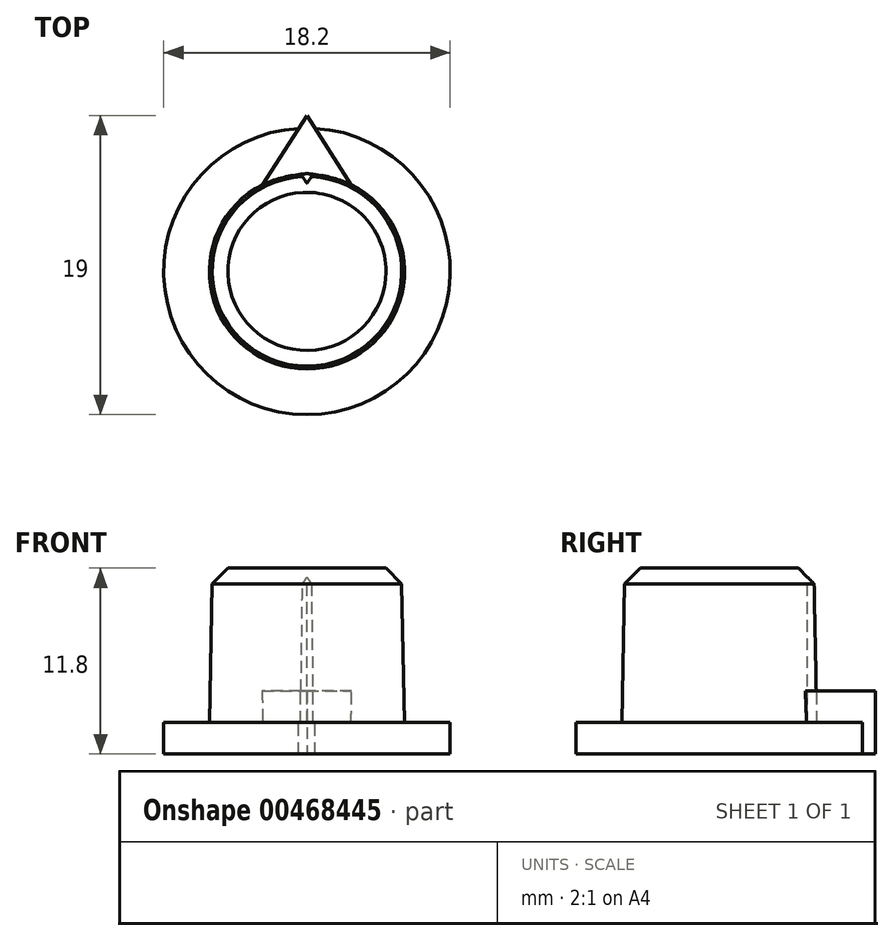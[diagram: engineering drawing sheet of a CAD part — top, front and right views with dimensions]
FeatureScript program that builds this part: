
annotation { "Feature Type Name" : "Feature", "Feature Type Description" : "" }
export const myFeature = defineFeature(function(context is Context, id is Id, definition is map)
    precondition{}
    {
        {
            var Q0;
            Q0=qCreatedBy(makeId("Right.planeOp"),FACE);
            var sketch = newSketch(context, id + "F0", { "sketchPlane" : qUnion([Q0])});
            skLineSegment(sketch, "E0", {"start": v(-9.1, 0) * mm, "end": v(-9.1, 2) * mm});
            skLineSegment(sketch, "E1", {"start": v(-9.1, 2) * mm, "end": v(-6.2, 2) * mm});
            skLineSegment(sketch, "E2", {"start": v(-6.2, 2) * mm, "end": v(-6.02, 10.8) * mm});
            skLineSegment(sketch, "E3", {"start": v(-5.02, 11.8) * mm, "end": v(0, 11.8) * mm});
            skLineSegment(sketch, "E4", {"start": v(0, 11.8) * mm, "end": v(0, 0) * mm});
            skLineSegment(sketch, "E5", {"start": v(0, 0) * mm, "end": v(-9.1, 0) * mm});
            skLineSegment(sketch, "E6", {"start": v(-6.02, 10.8) * mm, "end": v(-5.02, 11.8) * mm});
            skPoint(sketch, "E7.orphan", {"position": v(-6, 11.8) * mm});
            skSolve(sketch);
        }
        {
            var Q0;
            Q0=makeQuery(id+"F0.imprint","IMPRINT",FACE,{"disambiguationData":[TD([[makeQuery(id+"F0.imprint","IMPRINT",EDGE,{"derivedFrom":sQuery(id+"F0.wireOp",EDGE,"E0")}),-1.0]])]});
            var Q1;
            Q1=sQuery(id+"F0.wireOp",EDGE,"E4");
            revolve(context, id + "F1", {"entities" : qUnion([Q0]), "axis" : qUnion([Q1]), "revolveType" : RevolveType.FULL});
        }
        {
            var Q0;
            Q0=makeQuery(id+"F1.opRevolve","SWEPT_FACE",FACE,{"disambiguationData":[OSD([sQuery(id+"F0.wireOp",EDGE,"E3")])]});
            var sketch = newSketch(context, id + "F2", { "sketchPlane" : qUnion([Q0])});
            skLineSegment(sketch, "E8", {"start": v(0, 5.6) * mm, "end": v(-0.4, 6.19) * mm});
            skLineSegment(sketch, "E9", {"start": v(0.4, 6.19) * mm, "end": v(0, 5.6) * mm});
            skLineSegment(sketch, "E10", {"start": v(0, 0) * mm, "end": v(0, 6.2) * mm, "construction": true});
            skArc(sketch, "E11.2", {"start": v(0.4, 6.19) * mm, "mid": v(0, 6.2) * mm, "end": v(-0.4, 6.19) * mm});
            skSolve(sketch);
        }
        {
            var Q0;
            {var subQ0=sQuery(id+"F0.wireOp",EDGE,"E1");Q0=makeQuery(id+"Fq8YrrvR0LvIwax_1.47.F6.boolean.opBoolean","MERGE",FACE,{"derivedFrom":[makeQuery(id+"Fq8YrrvR0LvIwax_1.46.F6.boolean.opBoolean","MERGE",FACE,{"derivedFrom":[makeQuery(id+"Fq8YrrvR0LvIwax_1.45.F6.boolean.opBoolean","MERGE",FACE,{"derivedFrom":[makeQuery(id+"Fq8YrrvR0LvIwax_1.44.F6.boolean.opBoolean","MERGE",FACE,{"derivedFrom":[makeQuery(id+"Fq8YrrvR0LvIwax_1.43.F6.boolean.opBoolean","MERGE",FACE,{"derivedFrom":[makeQuery(id+"Fq8YrrvR0LvIwax_1.42.F6.boolean.opBoolean","MERGE",FACE,{"derivedFrom":[makeQuery(id+"Fq8YrrvR0LvIwax_1.41.F6.boolean.opBoolean","MERGE",FACE,{"derivedFrom":[makeQuery(id+"Fq8YrrvR0LvIwax_1.40.F6.boolean.opBoolean","MERGE",FACE,{"derivedFrom":[makeQuery(id+"Fq8YrrvR0LvIwax_1.39.F6.boolean.opBoolean","MERGE",FACE,{"derivedFrom":[makeQuery(id+"Fq8YrrvR0LvIwax_1.38.F6.boolean.opBoolean","MERGE",FACE,{"derivedFrom":[makeQuery(id+"Fq8YrrvR0LvIwax_1.37.F6.boolean.opBoolean","MERGE",FACE,{"derivedFrom":[makeQuery(id+"Fq8YrrvR0LvIwax_1.36.F6.boolean.opBoolean","MERGE",FACE,{"derivedFrom":[makeQuery(id+"Fq8YrrvR0LvIwax_1.35.F6.boolean.opBoolean","MERGE",FACE,{"derivedFrom":[makeQuery(id+"Fq8YrrvR0LvIwax_1.34.F6.boolean.opBoolean","MERGE",FACE,{"derivedFrom":[makeQuery(id+"Fq8YrrvR0LvIwax_1.33.F6.boolean.opBoolean","MERGE",FACE,{"derivedFrom":[makeQuery(id+"Fq8YrrvR0LvIwax_1.32.F6.boolean.opBoolean","MERGE",FACE,{"derivedFrom":[makeQuery(id+"Fq8YrrvR0LvIwax_1.31.F6.boolean.opBoolean","MERGE",FACE,{"derivedFrom":[makeQuery(id+"Fq8YrrvR0LvIwax_1.30.F6.boolean.opBoolean","MERGE",FACE,{"derivedFrom":[makeQuery(id+"Fq8YrrvR0LvIwax_1.29.F6.boolean.opBoolean","MERGE",FACE,{"derivedFrom":[makeQuery(id+"Fq8YrrvR0LvIwax_1.28.F6.boolean.opBoolean","MERGE",FACE,{"derivedFrom":[makeQuery(id+"Fq8YrrvR0LvIwax_1.27.F6.boolean.opBoolean","MERGE",FACE,{"derivedFrom":[makeQuery(id+"Fq8YrrvR0LvIwax_1.26.F6.boolean.opBoolean","MERGE",FACE,{"derivedFrom":[makeQuery(id+"Fq8YrrvR0LvIwax_1.25.F6.boolean.opBoolean","MERGE",FACE,{"derivedFrom":[makeQuery(id+"Fq8YrrvR0LvIwax_1.24.F6.boolean.opBoolean","MERGE",FACE,{"derivedFrom":[makeQuery(id+"Fq8YrrvR0LvIwax_1.23.F6.boolean.opBoolean","MERGE",FACE,{"derivedFrom":[makeQuery(id+"Fq8YrrvR0LvIwax_1.22.F6.boolean.opBoolean","MERGE",FACE,{"derivedFrom":[makeQuery(id+"Fq8YrrvR0LvIwax_1.21.F6.boolean.opBoolean","MERGE",FACE,{"derivedFrom":[makeQuery(id+"Fq8YrrvR0LvIwax_1.20.F6.boolean.opBoolean","MERGE",FACE,{"derivedFrom":[makeQuery(id+"Fq8YrrvR0LvIwax_1.19.F6.boolean.opBoolean","MERGE",FACE,{"derivedFrom":[makeQuery(id+"Fq8YrrvR0LvIwax_1.18.F6.boolean.opBoolean","MERGE",FACE,{"derivedFrom":[makeQuery(id+"Fq8YrrvR0LvIwax_1.17.F6.boolean.opBoolean","MERGE",FACE,{"derivedFrom":[makeQuery(id+"Fq8YrrvR0LvIwax_1.16.F6.boolean.opBoolean","MERGE",FACE,{"derivedFrom":[makeQuery(id+"Fq8YrrvR0LvIwax_1.15.F6.boolean.opBoolean","MERGE",FACE,{"derivedFrom":[makeQuery(id+"Fq8YrrvR0LvIwax_1.14.F6.boolean.opBoolean","MERGE",FACE,{"derivedFrom":[makeQuery(id+"Fq8YrrvR0LvIwax_1.13.F6.boolean.opBoolean","MERGE",FACE,{"derivedFrom":[makeQuery(id+"Fq8YrrvR0LvIwax_1.12.F6.boolean.opBoolean","MERGE",FACE,{"derivedFrom":[makeQuery(id+"Fq8YrrvR0LvIwax_1.11.F6.boolean.opBoolean","MERGE",FACE,{"derivedFrom":[makeQuery(id+"Fq8YrrvR0LvIwax_1.10.F6.boolean.opBoolean","MERGE",FACE,{"derivedFrom":[makeQuery(id+"Fq8YrrvR0LvIwax_1.9.F6.boolean.opBoolean","MERGE",FACE,{"derivedFrom":[makeQuery(id+"Fq8YrrvR0LvIwax_1.8.F6.boolean.opBoolean","MERGE",FACE,{"derivedFrom":[makeQuery(id+"Fq8YrrvR0LvIwax_1.7.F6.boolean.opBoolean","MERGE",FACE,{"derivedFrom":[makeQuery(id+"Fq8YrrvR0LvIwax_1.6.F6.boolean.opBoolean","MERGE",FACE,{"derivedFrom":[makeQuery(id+"Fq8YrrvR0LvIwax_1.5.F6.boolean.opBoolean","MERGE",FACE,{"derivedFrom":[makeQuery(id+"Fq8YrrvR0LvIwax_1.4.F6.boolean.opBoolean","MERGE",FACE,{"derivedFrom":[makeQuery(id+"Fq8YrrvR0LvIwax_1.3.F6.boolean.opBoolean","MERGE",FACE,{"derivedFrom":[makeQuery(id+"Fq8YrrvR0LvIwax_1.2.F6.boolean.opBoolean","MERGE",FACE,{"derivedFrom":[makeQuery(id+"Fq8YrrvR0LvIwax_1.1.F6.boolean.opBoolean","MERGE",FACE,{"derivedFrom":[makeQuery(id+"F6.boolean.opBoolean","MERGE",FACE,{"derivedFrom":[makeQuery(id+"F1.opRevolve","SWEPT_FACE",FACE,{"disambiguationData":[OSD([subQ0])]}),makeQuery(id+"F6.opExtrude","CAP_FACE",FACE,{"disambiguationData":[OSD([subQ0])],"isStart":false})]}),makeQuery(id+"Fq8YrrvR0LvIwax_1.1.F6.opExtrude","CAP_FACE",FACE,{"disambiguationData":[OSD([subQ0])],"isStart":false})]}),makeQuery(id+"Fq8YrrvR0LvIwax_1.2.F6.opExtrude","CAP_FACE",FACE,{"disambiguationData":[OSD([subQ0])],"isStart":false})]}),makeQuery(id+"Fq8YrrvR0LvIwax_1.3.F6.opExtrude","CAP_FACE",FACE,{"disambiguationData":[OSD([subQ0])],"isStart":false})]}),makeQuery(id+"Fq8YrrvR0LvIwax_1.4.F6.opExtrude","CAP_FACE",FACE,{"disambiguationData":[OSD([subQ0])],"isStart":false})]}),makeQuery(id+"Fq8YrrvR0LvIwax_1.5.F6.opExtrude","CAP_FACE",FACE,{"disambiguationData":[OSD([subQ0])],"isStart":false})]}),makeQuery(id+"Fq8YrrvR0LvIwax_1.6.F6.opExtrude","CAP_FACE",FACE,{"disambiguationData":[OSD([subQ0])],"isStart":false})]}),makeQuery(id+"Fq8YrrvR0LvIwax_1.7.F6.opExtrude","CAP_FACE",FACE,{"disambiguationData":[OSD([subQ0])],"isStart":false})]}),makeQuery(id+"Fq8YrrvR0LvIwax_1.8.F6.opExtrude","CAP_FACE",FACE,{"disambiguationData":[OSD([subQ0])],"isStart":false})]}),makeQuery(id+"Fq8YrrvR0LvIwax_1.9.F6.opExtrude","CAP_FACE",FACE,{"disambiguationData":[OSD([subQ0])],"isStart":false})]}),makeQuery(id+"Fq8YrrvR0LvIwax_1.10.F6.opExtrude","CAP_FACE",FACE,{"disambiguationData":[OSD([subQ0])],"isStart":false})]}),makeQuery(id+"Fq8YrrvR0LvIwax_1.11.F6.opExtrude","CAP_FACE",FACE,{"disambiguationData":[OSD([subQ0])],"isStart":false})]}),makeQuery(id+"Fq8YrrvR0LvIwax_1.12.F6.opExtrude","CAP_FACE",FACE,{"disambiguationData":[OSD([subQ0])],"isStart":false})]}),makeQuery(id+"Fq8YrrvR0LvIwax_1.13.F6.opExtrude","CAP_FACE",FACE,{"disambiguationData":[OSD([subQ0])],"isStart":false})]}),makeQuery(id+"Fq8YrrvR0LvIwax_1.14.F6.opExtrude","CAP_FACE",FACE,{"disambiguationData":[OSD([subQ0])],"isStart":false})]}),makeQuery(id+"Fq8YrrvR0LvIwax_1.15.F6.opExtrude","CAP_FACE",FACE,{"disambiguationData":[OSD([subQ0])],"isStart":false})]}),makeQuery(id+"Fq8YrrvR0LvIwax_1.16.F6.opExtrude","CAP_FACE",FACE,{"disambiguationData":[OSD([subQ0])],"isStart":false})]}),makeQuery(id+"Fq8YrrvR0LvIwax_1.17.F6.opExtrude","CAP_FACE",FACE,{"disambiguationData":[OSD([subQ0])],"isStart":false})]}),makeQuery(id+"Fq8YrrvR0LvIwax_1.18.F6.opExtrude","CAP_FACE",FACE,{"disambiguationData":[OSD([subQ0])],"isStart":false})]}),makeQuery(id+"Fq8YrrvR0LvIwax_1.19.F6.opExtrude","CAP_FACE",FACE,{"disambiguationData":[OSD([subQ0])],"isStart":false})]}),makeQuery(id+"Fq8YrrvR0LvIwax_1.20.F6.opExtrude","CAP_FACE",FACE,{"disambiguationData":[OSD([subQ0])],"isStart":false})]}),makeQuery(id+"Fq8YrrvR0LvIwax_1.21.F6.opExtrude","CAP_FACE",FACE,{"disambiguationData":[OSD([subQ0])],"isStart":false})]}),makeQuery(id+"Fq8YrrvR0LvIwax_1.22.F6.opExtrude","CAP_FACE",FACE,{"disambiguationData":[OSD([subQ0])],"isStart":false})]}),makeQuery(id+"Fq8YrrvR0LvIwax_1.23.F6.opExtrude","CAP_FACE",FACE,{"disambiguationData":[OSD([subQ0])],"isStart":false})]}),makeQuery(id+"Fq8YrrvR0LvIwax_1.24.F6.opExtrude","CAP_FACE",FACE,{"disambiguationData":[OSD([subQ0])],"isStart":false})]}),makeQuery(id+"Fq8YrrvR0LvIwax_1.25.F6.opExtrude","CAP_FACE",FACE,{"disambiguationData":[OSD([subQ0])],"isStart":false})]}),makeQuery(id+"Fq8YrrvR0LvIwax_1.26.F6.opExtrude","CAP_FACE",FACE,{"disambiguationData":[OSD([subQ0])],"isStart":false})]}),makeQuery(id+"Fq8YrrvR0LvIwax_1.27.F6.opExtrude","CAP_FACE",FACE,{"disambiguationData":[OSD([subQ0])],"isStart":false})]}),makeQuery(id+"Fq8YrrvR0LvIwax_1.28.F6.opExtrude","CAP_FACE",FACE,{"disambiguationData":[OSD([subQ0])],"isStart":false})]}),makeQuery(id+"Fq8YrrvR0LvIwax_1.29.F6.opExtrude","CAP_FACE",FACE,{"disambiguationData":[OSD([subQ0])],"isStart":false})]}),makeQuery(id+"Fq8YrrvR0LvIwax_1.30.F6.opExtrude","CAP_FACE",FACE,{"disambiguationData":[OSD([subQ0])],"isStart":false})]}),makeQuery(id+"Fq8YrrvR0LvIwax_1.31.F6.opExtrude","CAP_FACE",FACE,{"disambiguationData":[OSD([subQ0])],"isStart":false})]}),makeQuery(id+"Fq8YrrvR0LvIwax_1.32.F6.opExtrude","CAP_FACE",FACE,{"disambiguationData":[OSD([subQ0])],"isStart":false})]}),makeQuery(id+"Fq8YrrvR0LvIwax_1.33.F6.opExtrude","CAP_FACE",FACE,{"disambiguationData":[OSD([subQ0])],"isStart":false})]}),makeQuery(id+"Fq8YrrvR0LvIwax_1.34.F6.opExtrude","CAP_FACE",FACE,{"disambiguationData":[OSD([subQ0])],"isStart":false})]}),makeQuery(id+"Fq8YrrvR0LvIwax_1.35.F6.opExtrude","CAP_FACE",FACE,{"disambiguationData":[OSD([subQ0])],"isStart":false})]}),makeQuery(id+"Fq8YrrvR0LvIwax_1.36.F6.opExtrude","CAP_FACE",FACE,{"disambiguationData":[OSD([subQ0])],"isStart":false})]}),makeQuery(id+"Fq8YrrvR0LvIwax_1.37.F6.opExtrude","CAP_FACE",FACE,{"disambiguationData":[OSD([subQ0])],"isStart":false})]}),makeQuery(id+"Fq8YrrvR0LvIwax_1.38.F6.opExtrude","CAP_FACE",FACE,{"disambiguationData":[OSD([subQ0])],"isStart":false})]}),makeQuery(id+"Fq8YrrvR0LvIwax_1.39.F6.opExtrude","CAP_FACE",FACE,{"disambiguationData":[OSD([subQ0])],"isStart":false})]}),makeQuery(id+"Fq8YrrvR0LvIwax_1.40.F6.opExtrude","CAP_FACE",FACE,{"disambiguationData":[OSD([subQ0])],"isStart":false})]}),makeQuery(id+"Fq8YrrvR0LvIwax_1.41.F6.opExtrude","CAP_FACE",FACE,{"disambiguationData":[OSD([subQ0])],"isStart":false})]}),makeQuery(id+"Fq8YrrvR0LvIwax_1.42.F6.opExtrude","CAP_FACE",FACE,{"disambiguationData":[OSD([subQ0])],"isStart":false})]}),makeQuery(id+"Fq8YrrvR0LvIwax_1.43.F6.opExtrude","CAP_FACE",FACE,{"disambiguationData":[OSD([subQ0])],"isStart":false})]}),makeQuery(id+"Fq8YrrvR0LvIwax_1.44.F6.opExtrude","CAP_FACE",FACE,{"disambiguationData":[OSD([subQ0])],"isStart":false})]}),makeQuery(id+"Fq8YrrvR0LvIwax_1.45.F6.opExtrude","CAP_FACE",FACE,{"disambiguationData":[OSD([subQ0])],"isStart":false})]}),makeQuery(id+"Fq8YrrvR0LvIwax_1.46.F6.opExtrude","CAP_FACE",FACE,{"disambiguationData":[OSD([subQ0])],"isStart":false})]}),makeQuery(id+"Fq8YrrvR0LvIwax_1.47.F6.opExtrude","CAP_FACE",FACE,{"disambiguationData":[OSD([subQ0])],"isStart":false})]});}
            var sketch = newSketch(context, id + "F3", { "sketchPlane" : qUnion([Q0])});
            skLineSegment(sketch, "E12", {"start": v(-3.8, 3.98) * mm, "end": v(0, 9.9) * mm});
            skLineSegment(sketch, "E13", {"start": v(0, 9.9) * mm, "end": v(3.8, 3.98) * mm});
            skLineSegment(sketch, "E14", {"start": v(0, 0) * mm, "end": v(0, 9.9) * mm, "construction": true});
            skArc(sketch, "E15", {"start": v(3.8, 3.98) * mm, "mid": v(0, 5.5) * mm, "end": v(-3.8, 3.98) * mm});
            skSolve(sketch);
        }
        {
            var Q0;
            Q0 = qSketchRegion(id + "F3", true);
            extrude(context, id + "F4", {"entities" : qUnion([Q0]), "operationType" : NewBodyOperationType.ADD, "depth" : 2 * mm});
        }
        {
            var Q0;
            Q0 = qSketchRegion(id + "F3", true);
            var Q1;
            Q1=makeQuery(id+"F1.opRevolve","SWEPT_FACE",FACE,{"disambiguationData":[OSD([sQuery(id+"F0.wireOp",EDGE,"E5")])]});
            extrude(context, id + "F5", {"entities" : qUnion([Q0]), "operationType" : NewBodyOperationType.ADD, "endBound" : BoundingType.UP_TO_SURFACE, "oppositeDirection" : true, "endBoundEntityFace" : qUnion([Q1]), "depth" : 25 * mm});
        }
        {
            var Q0;
            Q0 = qSketchRegion(id + "F2", true);
            var Q1;
            Q1=makeQuery(id+"F1.opRevolve","SWEPT_FACE",FACE,{"disambiguationData":[OSD([sQuery(id+"F0.wireOp",EDGE,"E1")])]});
            extrude(context, id + "F6", {"entities" : qUnion([Q0]), "operationType" : NewBodyOperationType.REMOVE, "endBound" : BoundingType.UP_TO_SURFACE, "oppositeDirection" : true, "endBoundEntityFace" : qUnion([Q1]), "depth" : 25 * mm});
        }
    });
